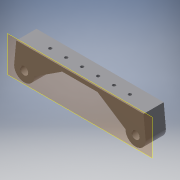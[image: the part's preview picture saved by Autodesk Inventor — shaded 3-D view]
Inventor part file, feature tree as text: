
AUTODESK INVENTOR PART (.ipt)
format: ipt  version: 2016 (Build 200138000, 138)  size: 172,544 bytes
history: native  units: in
note: dims shown in document units (in); Inventor stores cm internally (conversion verified against a paired STEP export)
features: extrude x4, sketch x4, reference x2, projected_geometry x2, plane x1
ambient origin geometry x8: Origin, YZ Plane, XZ Plane, XY Plane, X Axis, Y Axis, Z Axis, Center Point
bodies: Solid1 (feature_tree)
feature tree (13):
  plane  "Work Plane1"
  extrude  "Extrusion1"  Depth=0.3937in
  extrude  "Extrusion2"  Depth=0.0394in TaperAngle=0.0deg
  extrude  "Extrusion3"  Depth=0.1575in
  extrude  "Extrusion4"  Depth=0.2in
  sketch  "Sketch1"  dims[d0=1.0in d1=0.0in d2=0.3937in]
  reference  "Reference1"
  sketch  "Sketch2"  dims[d3=0.3937in d4=0.0394in d5=0.0in]
  projected_geometry  "Projected Loop1"
  sketch  "Sketch3"  dims[d6=1.1811in d9=0.1575in]
  reference  "Reference2"
  sketch  "Sketch4"  dims[d10=0.1575in d11=0.1575in d12=20.0in d13=0.0in d14=0.2in d15=0.0in]
  projected_geometry  "Projected Loop2"
